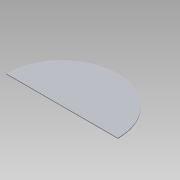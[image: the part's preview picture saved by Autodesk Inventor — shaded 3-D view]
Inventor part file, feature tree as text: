
AUTODESK INVENTOR PART (.ipt)
format: ipt  version: 2015 SP1 (Build 190203100, 203)  size: 76,288 bytes
history: native  units: mm
features: extrude x1, sketch x1
ambient origin geometry x8: Origin, YZ Plane, XZ Plane, XY Plane, X Axis, Y Axis, Z Axis, Center Point
bodies: Solid1 (feature_tree)
feature tree (2):
  extrude  "Extrusion1"  TaperAngle=180.0deg  [1 undecoded]
  sketch  "Sketch1"  dims[d0=300.0mm d1=180.0deg d2=4.0mm d3=0.0mm]
note: 1 required parameter value undecoded (feature->parameter linkage not recoverable at this tier; creation-order binding heuristic only, values carry confidence <= 0.55)
